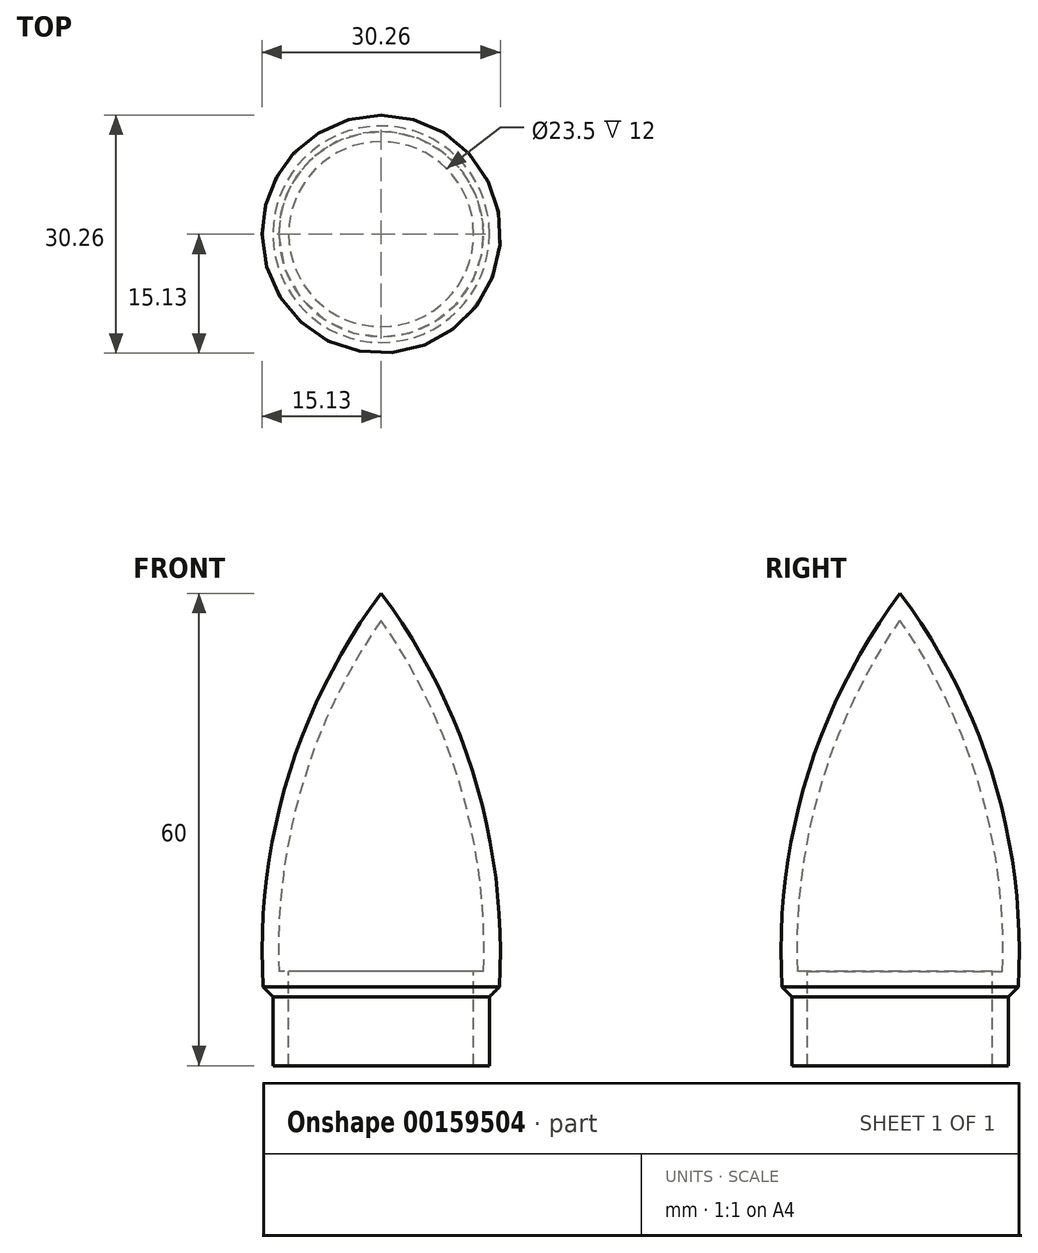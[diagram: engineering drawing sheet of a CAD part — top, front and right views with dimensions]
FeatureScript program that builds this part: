
annotation { "Feature Type Name" : "Feature", "Feature Type Description" : "" }
export const myFeature = defineFeature(function(context is Context, id is Id, definition is map)
    precondition{}
    {
        {
            var Q0;
            Q0=qCreatedBy(makeId("Right.planeOp"),FACE);
            var sketch = newSketch(context, id + "F0", { "sketchPlane" : qUnion([Q0])});
            skLineSegment(sketch, "E0", {"start": v(0, 23.46) * mm, "end": v(0, -25.54) * mm});
            skLineSegment(sketch, "E1", {"start": v(-13.75, 0) * mm, "end": v(-13.75, 10) * mm});
            skLineSegment(sketch, "E2", {"start": v(-13.75, 10) * mm, "end": v(-15, 10) * mm});
            skLineSegment(sketch, "E3", {"start": v(-13.75, 0) * mm, "end": v(-11.75, 0) * mm});
            skLineSegment(sketch, "E4", {"start": v(-11.75, 0) * mm, "end": v(-11.75, 12) * mm});
            skLineSegment(sketch, "E5", {"start": v(-11.75, 12) * mm, "end": v(-13, 12) * mm});
            skLineSegment(sketch, "E6", {"start": v(0, 60) * mm, "end": v(0, 56.58) * mm});
            skArc(sketch, "E7", {"start": v(0, 60) * mm, "mid": v(-11.93, 36.33) * mm, "end": v(-15, 10) * mm});
            skArc(sketch, "E8", {"start": v(0, 56.58) * mm, "mid": v(-10.11, 35.34) * mm, "end": v(-13, 12) * mm});
            skLineSegment(sketch, "E9", {"start": v(-15, 10) * mm, "end": v(-13.75, 8.75) * mm});
            skSolve(sketch);
        }
        {
            var Q0;
            Q0=qCreatedBy(makeId("Right.planeOp"),FACE);
            var sketch = newSketch(context, id + "F1", { "sketchPlane" : qUnion([Q0])});
            skLineSegment(sketch, "E10", {"start": v(0, 79.84) * mm, "end": v(0, -8.1) * mm, "construction": true});
            skSolve(sketch);
        }
        {
            var Q0;
            Q0 = qSketchRegion(id + "F0", true);
            var Q1;
            Q1 = qConstructionFilter(qBodyType(qCreatedBy(id + "F0" ,EDGE), BodyType.WIRE), ConstructionObject.NO);
            var Q2;
            Q2=sQuery(id+"F1.wireOp",EDGE,"E10");
            revolve(context, id + "F2", {"entities" : qUnion([Q0]), "surfaceEntities" : qUnion([Q1]), "axis" : qUnion([Q2]), "revolveType" : RevolveType.FULL});
        }
    });
